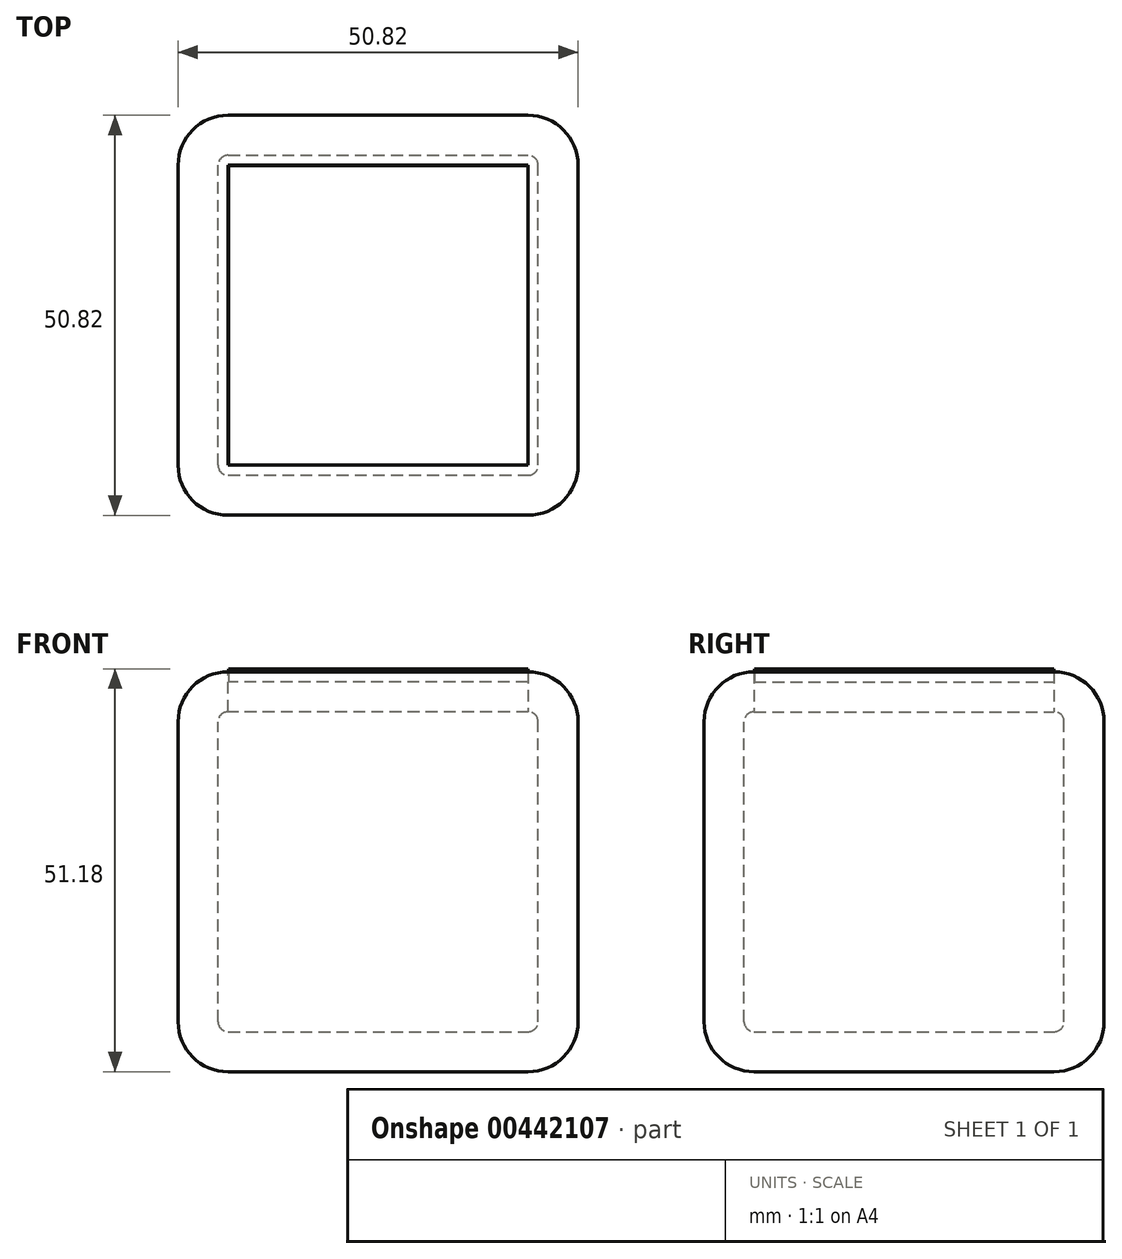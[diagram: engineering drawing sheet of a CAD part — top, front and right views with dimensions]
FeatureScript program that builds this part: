
annotation { "Feature Type Name" : "Feature", "Feature Type Description" : "" }
export const myFeature = defineFeature(function(context is Context, id is Id, definition is map)
    precondition{}
    {
        {
            var Q0;
            Q0=qCreatedBy(makeId("Top.planeOp"),FACE);
            var sketch = newSketch(context, id + "F0", { "sketchPlane" : qUnion([Q0])});
            skLineSegment(sketch, "E0.bottom", {"start": v(-25.4, -25.4) * mm, "end": v(25.4, -25.4) * mm});
            skLineSegment(sketch, "E0.top", {"start": v(-25.4, 25.4) * mm, "end": v(25.4, 25.4) * mm});
            skLineSegment(sketch, "E0.left", {"start": v(-25.4, -25.4) * mm, "end": v(-25.4, 25.4) * mm});
            skLineSegment(sketch, "E0.right", {"start": v(25.4, -25.4) * mm, "end": v(25.4, 25.4) * mm});
            skPoint(sketch, "E0.middle", {"position": v(0, 0) * mm});
            skSolve(sketch);
        }
        {
            var Q0;
            Q0 = qSketchRegion(id + "F0", true);
            extrude(context, id + "F1", {"entities" : qUnion([Q0]), "depth" : 50.8 * mm});
        }
        {
            var Q0;
            Q0=makeQuery(id+"F1.opExtrude","CAP_EDGE",EDGE,{"disambiguationData":[OSD([sQuery(id+"F0.wireOp",EDGE,"E0.bottom")])],"isStart":false});
            var Q1;
            Q1=makeQuery(id+"F1.opExtrude","CAP_EDGE",EDGE,{"disambiguationData":[OSD([sQuery(id+"F0.wireOp",EDGE,"E0.right")])],"isStart":false});
            var Q2;
            Q2=makeQuery(id+"F1.opExtrude","SWEPT_EDGE",EDGE,{"disambiguationData":[OSD([sQuery(id+"F0.wireOp",EDGE,"E0.bottom"),sQuery(id+"F0.wireOp",EDGE,"E0.right")])]});
            var Q3;
            Q3=makeQuery(id+"F1.opExtrude","SWEPT_EDGE",EDGE,{"disambiguationData":[OSD([sQuery(id+"F0.wireOp",EDGE,"E0.top"),sQuery(id+"F0.wireOp",EDGE,"E0.right")])]});
            var Q4;
            Q4=makeQuery(id+"F1.opExtrude","CAP_EDGE",EDGE,{"disambiguationData":[OSD([sQuery(id+"F0.wireOp",EDGE,"E0.right")])],"isStart":true});
            var Q5;
            Q5=makeQuery(id+"F1.opExtrude","CAP_EDGE",EDGE,{"disambiguationData":[OSD([sQuery(id+"F0.wireOp",EDGE,"E0.bottom")])],"isStart":true});
            var Q6;
            Q6=makeQuery(id+"F1.opExtrude","CAP_EDGE",EDGE,{"disambiguationData":[OSD([sQuery(id+"F0.wireOp",EDGE,"E0.left")])],"isStart":false});
            var Q7;
            Q7=makeQuery(id+"F1.opExtrude","CAP_EDGE",EDGE,{"disambiguationData":[OSD([sQuery(id+"F0.wireOp",EDGE,"E0.top")])],"isStart":false});
            var Q8;
            Q8=makeQuery(id+"F1.opExtrude","SWEPT_EDGE",EDGE,{"disambiguationData":[OSD([sQuery(id+"F0.wireOp",EDGE,"E0.bottom"),sQuery(id+"F0.wireOp",EDGE,"E0.left")])]});
            var Q9;
            Q9=makeQuery(id+"F1.opExtrude","SWEPT_EDGE",EDGE,{"disambiguationData":[OSD([sQuery(id+"F0.wireOp",EDGE,"E0.top"),sQuery(id+"F0.wireOp",EDGE,"E0.left")])]});
            var Q10;
            Q10=makeQuery(id+"F1.opExtrude","CAP_EDGE",EDGE,{"disambiguationData":[OSD([sQuery(id+"F0.wireOp",EDGE,"E0.top")])],"isStart":true});
            var Q11;
            Q11=makeQuery(id+"F1.opExtrude","CAP_EDGE",EDGE,{"disambiguationData":[OSD([sQuery(id+"F0.wireOp",EDGE,"E0.left")])],"isStart":true});
            fillet(context, id + "F2", {"entities" : qUnion([Q0, Q1, Q2, Q3, Q4, Q5, Q6, Q7, Q8, Q9, Q10, Q11]), "radius" : 6.35 * mm, "tangentPropagation" : true, "allowEdgeOverflow" : false});
        }
        {
            var Q0;
            Q0=makeQuery(id+"F1.opExtrude","CAP_FACE",FACE,{"disambiguationData":[OSD([sQuery(id+"F0.wireOp",EDGE,"E0.bottom"),sQuery(id+"F0.wireOp",EDGE,"E0.top"),sQuery(id+"F0.wireOp",EDGE,"E0.left"),sQuery(id+"F0.wireOp",EDGE,"E0.right")])],"isStart":false});
            shell(context, id + "F3", {"entities" : qUnion([Q0]), "thickness" : 5.08 * mm});
        }
        {
            var Q0;
            Q0=qCreatedBy(makeId("Top.planeOp"),FACE);
            var sketch = newSketch(context, id + "F4", { "sketchPlane" : qUnion([Q0])});
            skLineSegment(sketch, "E1.bottom", {"start": v(19.01, -19.03) * mm, "end": v(-19.01, -19.03) * mm});
            skLineSegment(sketch, "E1.top", {"start": v(19.01, 19.03) * mm, "end": v(-19.01, 19.03) * mm});
            skLineSegment(sketch, "E1.left", {"start": v(19.01, -19.03) * mm, "end": v(19.01, 19.03) * mm});
            skLineSegment(sketch, "E1.right", {"start": v(-19.01, -19.03) * mm, "end": v(-19.01, 19.03) * mm});
            skPoint(sketch, "E1.middle", {"position": v(0, 0) * mm});
            skSolve(sketch);
        }
        {
            var Q0;
            Q0 = qSketchRegion(id + "F4", true);
            extrude(context, id + "F5", {"entities" : qUnion([Q0]), "depth" : 51.18 * mm, "hasSecondDirection" : true, "secondDirectionOppositeDirection" : true, "secondDirectionDepth" : -49.53 * mm});
        }
    });
